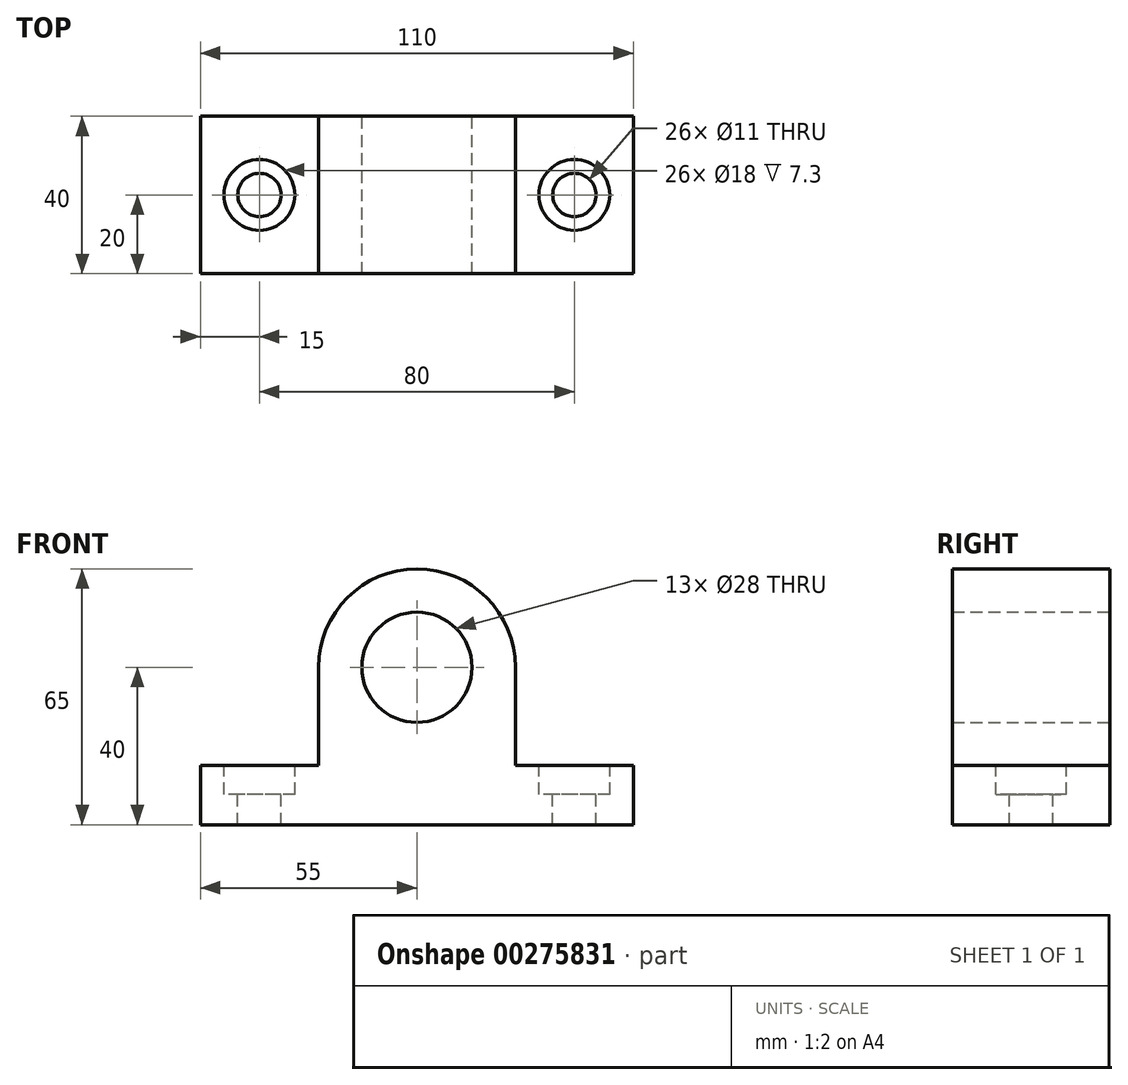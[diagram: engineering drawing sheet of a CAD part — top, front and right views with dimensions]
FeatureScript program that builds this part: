
annotation { "Feature Type Name" : "Feature", "Feature Type Description" : "" }
export const myFeature = defineFeature(function(context is Context, id is Id, definition is map)
    precondition{}
    {
        {
            var Q0;
            Q0=qCreatedBy(makeId("Front.planeOp"),FACE);
            var sketch = newSketch(context, id + "F0", { "sketchPlane" : qUnion([Q0])});
            skLineSegment(sketch, "E0.top", {"start": v(-55, -32.5) * mm, "end": v(55, -32.5) * mm});
            skLineSegment(sketch, "E0.left", {"start": v(-55, -17.5) * mm, "end": v(-55, -32.5) * mm});
            skLineSegment(sketch, "E1.top", {"start": v(-55, -17.5) * mm, "end": v(-25, -17.5) * mm});
            skLineSegment(sketch, "E1.right", {"start": v(-25, 7.5) * mm, "end": v(-25, -17.5) * mm});
            skLineSegment(sketch, "E2.top", {"start": v(55, -17.5) * mm, "end": v(25, -17.5) * mm});
            skLineSegment(sketch, "E2.right", {"start": v(25, 7.5) * mm, "end": v(25, -17.5) * mm});
            skArc(sketch, "E3", {"start": v(25, 7.5) * mm, "mid": v(0, 32.5) * mm, "end": v(-25, 7.5) * mm});
            skLineSegment(sketch, "E4", {"start": v(55, -17.5) * mm, "end": v(55, -32.5) * mm});
            skCircle(sketch, "E5", {"center": v(0, 7.5) * mm, "radius": 14 * mm});
            skSolve(sketch);
        }
        {
            var Q0;
            Q0=makeQuery(id+"F0.imprint","IMPRINT",FACE,{"disambiguationData":[TD([[makeQuery(id+"F0.imprint","IMPRINT",EDGE,{"derivedFrom":sQuery(id+"F0.wireOp",EDGE,"E0.top")}),1.0]])]});
            extrude(context, id + "F1", {"entities" : qUnion([Q0]), "depth" : 40 * mm});
        }
        {
            var Q0;
            Q0=makeQuery(id+"F1.opExtrude","SWEPT_FACE",FACE,{"disambiguationData":[OSD([sQuery(id+"F0.wireOp",EDGE,"E1.top")])]});
            var sketch = newSketch(context, id + "F2", { "sketchPlane" : qUnion([Q0])});
            skCircle(sketch, "E6", {"center": v(-40, -20) * mm, "radius": 9 * mm});
            skCircle(sketch, "E7", {"center": v(-40, -20) * mm, "radius": 5.5 * mm});
            skSolve(sketch);
        }
        {
            var Q0;
            Q0=makeQuery(id+"F1.opExtrude","SWEPT_FACE",FACE,{"disambiguationData":[OSD([sQuery(id+"F0.wireOp",EDGE,"E2.top")])]});
            var sketch = newSketch(context, id + "F3", { "sketchPlane" : qUnion([Q0])});
            skCircle(sketch, "E8", {"center": v(40, -20) * mm, "radius": 9 * mm});
            skCircle(sketch, "E9", {"center": v(40, -20) * mm, "radius": 5.5 * mm});
            skSolve(sketch);
        }
        {
            var Q0;
            Q0=makeQuery(id+"F2.imprint","IMPRINT",FACE,{"disambiguationData":[TD([[makeQuery(id+"F2.imprint","IMPRINT",EDGE,{"derivedFrom":sQuery(id+"F2.wireOp",EDGE,"E7")}),1.0]])]});
            var Q1;
            Q1=makeQuery(id+"F3.imprint","IMPRINT",FACE,{"disambiguationData":[TD([[makeQuery(id+"F3.imprint","IMPRINT",EDGE,{"derivedFrom":sQuery(id+"F3.wireOp",EDGE,"E9")}),1.0]])]});
            extrude(context, id + "F4", {"entities" : qUnion([Q0, Q1]), "operationType" : NewBodyOperationType.REMOVE, "oppositeDirection" : true, "depth" : 15 * mm});
        }
        {
            var Q0;
            Q0=makeQuery(id+"F2.imprint","IMPRINT",FACE,{"disambiguationData":[TD([[makeQuery(id+"F2.imprint","IMPRINT",EDGE,{"derivedFrom":sQuery(id+"F2.wireOp",EDGE,"E6")}),1.0]])]});
            var Q1;
            Q1=makeQuery(id+"F3.imprint","IMPRINT",FACE,{"disambiguationData":[TD([[makeQuery(id+"F3.imprint","IMPRINT",EDGE,{"derivedFrom":sQuery(id+"F3.wireOp",EDGE,"E8")}),1.0]])]});
            extrude(context, id + "F5", {"entities" : qUnion([Q0, Q1]), "operationType" : NewBodyOperationType.REMOVE, "oppositeDirection" : true, "depth" : 7.3 * mm});
        }
    });
